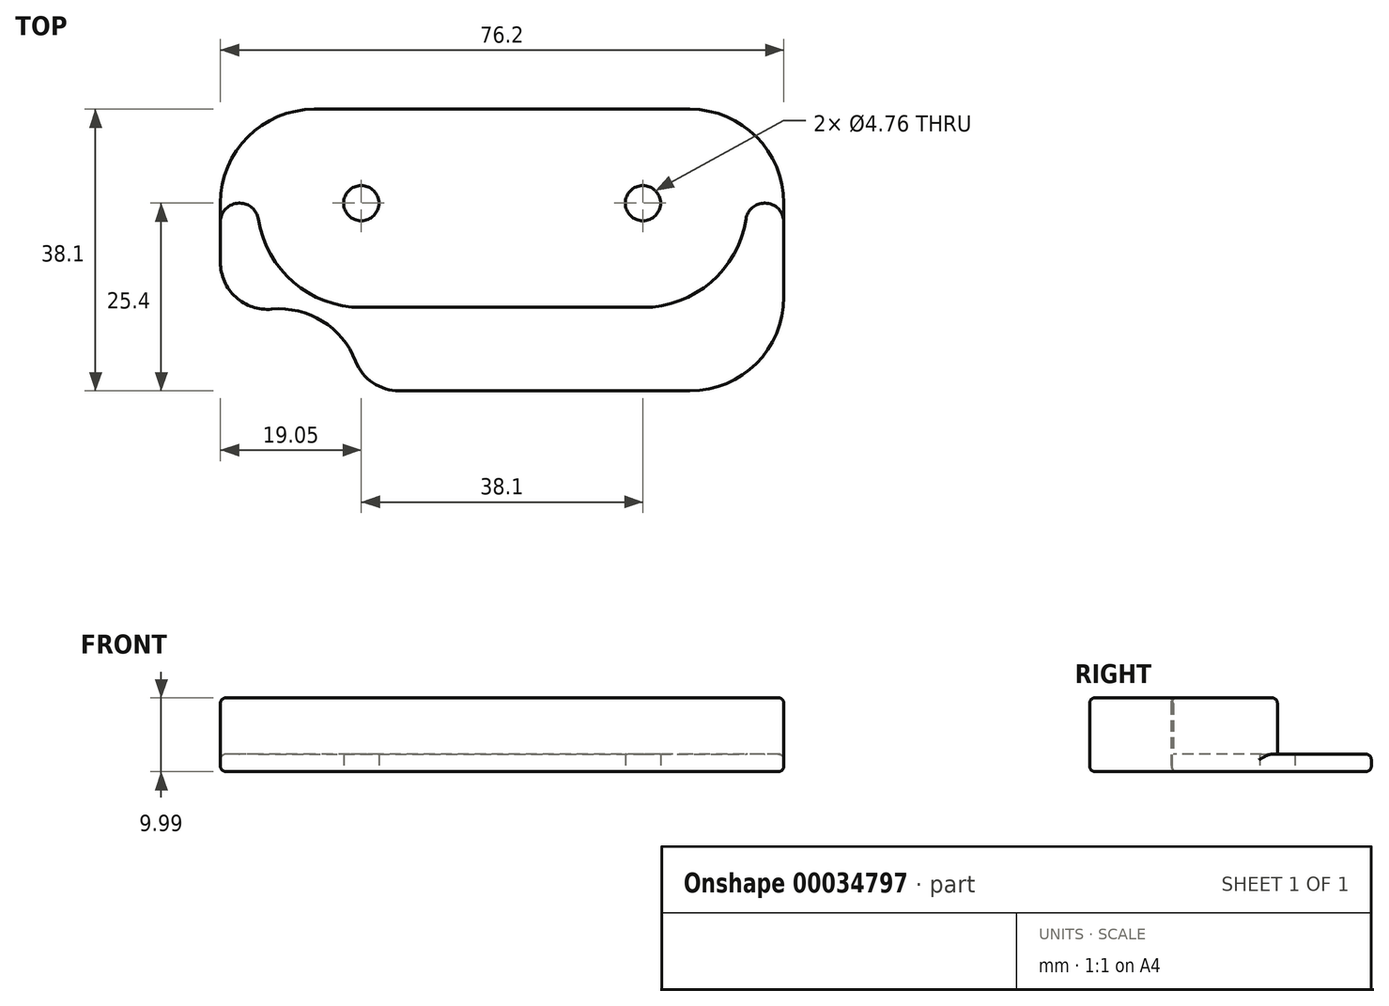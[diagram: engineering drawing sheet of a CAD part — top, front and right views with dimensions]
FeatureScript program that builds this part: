
annotation { "Feature Type Name" : "Feature", "Feature Type Description" : "" }
export const myFeature = defineFeature(function(context is Context, id is Id, definition is map)
    precondition{}
    {
        {
            var Q0;
            Q0=qCreatedBy(makeId("Top.planeOp"),FACE);
            var sketch = newSketch(context, id + "F0", { "sketchPlane" : qUnion([Q0])});
            skLineSegment(sketch, "E0.rect.bottom", {"start": v(25.4, 19.05) * mm, "end": v(-25.4, 19.05) * mm});
            skLineSegment(sketch, "E0.rect.top", {"start": v(25.4, -19.05) * mm, "end": v(-25.4, -19.05) * mm});
            skLineSegment(sketch, "E0.rect.left", {"start": v(38.1, 6.35) * mm, "end": v(38.1, -6.35) * mm});
            skLineSegment(sketch, "E0.rect.right", {"start": v(-38.1, 6.35) * mm, "end": v(-38.1, -6.35) * mm});
            skPoint(sketch, "E0.rect.middle", {"position": v(0, 0) * mm});
            skCircle(sketch, "E1", {"center": v(-19.05, 6.35) * mm, "radius": 13.84 * mm, "construction": true});
            skCircle(sketch, "E2", {"center": v(19.05, 6.35) * mm, "radius": 13.84 * mm, "construction": true});
            skLineSegment(sketch, "E3", {"start": v(-19.05, 6.35) * mm, "end": v(19.05, 6.35) * mm, "construction": true});
            skLineSegment(sketch, "E4", {"start": v(0, 6.35) * mm, "end": v(0, 0) * mm, "construction": true});
            skPoint(sketch, "E5.visualSharp", {"position": v(-38.1, 19.05) * mm});
            skArc(sketch, "E5.filletArc", {"start": v(-25.4, 19.05) * mm, "mid": v(-34.38, 15.33) * mm, "end": v(-38.1, 6.35) * mm});
            skPoint(sketch, "E6.visualSharp", {"position": v(-38.1, -19.05) * mm});
            skArc(sketch, "E6.filletArc", {"start": v(-38.1, -6.35) * mm, "mid": v(-34.38, -15.33) * mm, "end": v(-25.4, -19.05) * mm});
            skPoint(sketch, "E7.visualSharp", {"position": v(38.1, -19.05) * mm});
            skArc(sketch, "E7.filletArc", {"start": v(25.4, -19.05) * mm, "mid": v(34.38, -15.33) * mm, "end": v(38.1, -6.35) * mm});
            skPoint(sketch, "E8.visualSharp", {"position": v(38.1, 19.05) * mm});
            skArc(sketch, "E8.filletArc", {"start": v(38.1, 6.35) * mm, "mid": v(34.38, 15.33) * mm, "end": v(25.4, 19.05) * mm});
            skCircle(sketch, "E9", {"center": v(-19.05, 6.35) * mm, "radius": 2.38 * mm});
            skCircle(sketch, "E10", {"center": v(19.05, 6.35) * mm, "radius": 2.38 * mm});
            skSolve(sketch);
        }
        {
            var Q0;
            Q0=makeQuery(id+"F0.imprint","IMPRINT",FACE,{"disambiguationData":[TD([[makeQuery(id+"F0.imprint","IMPRINT",EDGE,{"derivedFrom":sQuery(id+"F0.wireOp",EDGE,"E0.rect.bottom")}),1.0]])]});
            extrude(context, id + "F1", {"entities" : qUnion([Q0]), "depth" : 2.37 * mm});
        }
        {
            var Q0;
            Q0=makeQuery(id+"F1.opExtrude","CAP_FACE",FACE,{"disambiguationData":[OSD([sQuery(id+"F0.wireOp",EDGE,"E0.rect.bottom"),sQuery(id+"F0.wireOp",EDGE,"E0.rect.top"),sQuery(id+"F0.wireOp",EDGE,"E0.rect.left"),sQuery(id+"F0.wireOp",EDGE,"E0.rect.right"),sQuery(id+"F0.wireOp",EDGE,"E5.filletArc"),sQuery(id+"F0.wireOp",EDGE,"E6.filletArc"),sQuery(id+"F0.wireOp",EDGE,"E7.filletArc"),sQuery(id+"F0.wireOp",EDGE,"E8.filletArc")])],"isStart":false});
            var sketch = newSketch(context, id + "F2", { "sketchPlane" : qUnion([Q0])});
            skArc(sketch, "E11", {"start": v(-32.98, 4.2) * mm, "mid": v(-28.23, -4.35) * mm, "end": v(-19.05, -7.75) * mm});
            skArc(sketch, "E12", {"start": v(19.05, -7.75) * mm, "mid": v(28.23, -4.35) * mm, "end": v(32.98, 4.2) * mm});
            skLineSegment(sketch, "E13", {"start": v(-19.05, -7.75) * mm, "end": v(19.05, -7.75) * mm});
            skLineSegment(sketch, "E14", {"start": v(-35.56, 6.35) * mm, "end": v(-35.5, 6.35) * mm});
            skLineSegment(sketch, "E15.trimOffspring", {"start": v(35.5, 6.35) * mm, "end": v(35.56, 6.35) * mm});
            skLineSegment(sketch, "E16.0", {"start": v(38.1, 3.81) * mm, "end": v(38.1, -6.35) * mm});
            skArc(sketch, "E16.1", {"start": v(25.4, -19.05) * mm, "mid": v(34.38, -15.33) * mm, "end": v(38.1, -6.35) * mm});
            skLineSegment(sketch, "E16.2", {"start": v(25.4, -19.05) * mm, "end": v(-25.4, -19.05) * mm});
            skArc(sketch, "E16.3", {"start": v(-38.1, -6.35) * mm, "mid": v(-34.38, -15.33) * mm, "end": v(-25.4, -19.05) * mm});
            skLineSegment(sketch, "E16.4", {"start": v(-38.1, 3.8) * mm, "end": v(-38.1, -6.35) * mm});
            skLineSegment(sketch, "E17", {"start": v(-62.67, 14.6) * mm, "end": v(-70.33, 1.23) * mm});
            skLineSegment(sketch, "E18", {"start": v(-61.8, 15.21) * mm, "end": v(-36.93, 19.75) * mm});
            skPoint(sketch, "E19.visualSharp", {"position": v(-62.38, 15.1) * mm});
            skArc(sketch, "E19.filletArc", {"start": v(-61.8, 15.21) * mm, "mid": v(-62.3, 15) * mm, "end": v(-62.67, 14.6) * mm});
            skPoint(sketch, "E20.visualSharp", {"position": v(-38.1, 6.35) * mm});
            skArc(sketch, "E20.filletArc", {"start": v(-35.56, 6.35) * mm, "mid": v(-37.36, 5.6) * mm, "end": v(-38.1, 3.8) * mm});
            skPoint(sketch, "E21.visualSharp", {"position": v(-33.15, 6.35) * mm});
            skArc(sketch, "E21.filletArc", {"start": v(-32.98, 4.2) * mm, "mid": v(-33.84, 5.74) * mm, "end": v(-35.5, 6.35) * mm});
            skPoint(sketch, "E22.visualSharp", {"position": v(33.15, 6.35) * mm});
            skArc(sketch, "E22.filletArc", {"start": v(35.5, 6.35) * mm, "mid": v(33.84, 5.74) * mm, "end": v(32.98, 4.2) * mm});
            skPoint(sketch, "E23.visualSharp", {"position": v(38.1, 6.35) * mm});
            skArc(sketch, "E23.filletArc", {"start": v(38.1, 3.81) * mm, "mid": v(37.36, 5.6) * mm, "end": v(35.56, 6.35) * mm});
            skSolve(sketch);
        }
        {
            var Q0;
            Q0 = qSketchRegion(id + "F2", true);
            extrude(context, id + "F3", {"entities" : qUnion([Q0]), "operationType" : NewBodyOperationType.ADD, "depth" : 7.62 * mm});
        }
        {
            var Q0;
            Q0=qCreatedBy(makeId("Top.planeOp"),FACE);
            var sketch = newSketch(context, id + "F4", { "sketchPlane" : qUnion([Q0])});
            skCircle(sketch, "E24.0", {"center": v(-19.05, 6.35) * mm, "radius": 2.38 * mm, "construction": true});
            skCircle(sketch, "E24.1", {"center": v(19.05, 6.35) * mm, "radius": 2.38 * mm, "construction": true});
            skLineSegment(sketch, "E25", {"start": v(-19.05, 6.35) * mm, "end": v(-19.05, -19.05) * mm, "construction": true});
            skLineSegment(sketch, "E26", {"start": v(-19.05, -19.05) * mm, "end": v(-30.16, -19.05) * mm, "construction": true});
            skCircle(sketch, "E27", {"center": v(-30.16, -19.05) * mm, "radius": 11.11 * mm});
            skLineSegment(sketch, "E28", {"start": v(0, 0) * mm, "end": v(0, -31.17) * mm, "construction": true});
            skLineSegment(sketch, "E29.MirrorCS", {"start": v(19.05, -19.05) * mm, "end": v(30.16, -19.05) * mm, "construction": true});
            skLineSegment(sketch, "E30.MirrorCS", {"start": v(19.05, 6.35) * mm, "end": v(19.05, -19.05) * mm, "construction": true});
            skCircle(sketch, "E31.MirrorC", {"center": v(30.16, -19.05) * mm, "radius": 11.11 * mm});
            skSolve(sketch);
        }
        {
            var Q0;
            Q0=makeQuery(id+"F4.imprint","IMPRINT",FACE,{"disambiguationData":[TD([[makeQuery(id+"F4.imprint","IMPRINT",EDGE,{"derivedFrom":sQuery(id+"F4.wireOp",EDGE,"E27")}),1.0]])]});
            var Q1;
            Q1=makeQuery(id+"F4.imprint","IMPRINT",FACE,{"disambiguationData":[TD([[makeQuery(id+"F4.imprint","IMPRINT",EDGE,{"derivedFrom":sQuery(id+"F4.wireOp",EDGE,"E31.MirrorC")}),-1.0]])]});
            extrude(context, id + "F5", {"entities" : qUnion([Q0, Q1]), "operationType" : NewBodyOperationType.REMOVE, "depth" : 25.4 * mm});
        }
        {
            var Q0;
            Q0=makeQuery(id+"F5.boolean.opBoolean","INTERSECT",EDGE,{"derivedFrom":[makeQuery(id+"F3.boolean.opBoolean","MERGE",FACE,{"derivedFrom":[makeQuery(id+"F1.opExtrude","SWEPT_FACE",FACE,{"disambiguationData":[OSD([sQuery(id+"F0.wireOp",EDGE,"E6.filletArc")])]}),makeQuery(id+"F3.opExtrude","SWEPT_FACE",FACE,{"disambiguationData":[OSD([sQuery(id+"F2.wireOp",EDGE,"E16.3")])]})]}),makeQuery(id+"F5.opExtrude","SWEPT_FACE",FACE,{"disambiguationData":[OSD([sQuery(id+"F4.wireOp",EDGE,"E27")])]})]});
            var Q1;
            Q1=makeQuery(id+"F5.boolean.opBoolean","INTERSECT",EDGE,{"derivedFrom":[makeQuery(id+"F3.boolean.opBoolean","MERGE",FACE,{"derivedFrom":[makeQuery(id+"F1.opExtrude","SWEPT_FACE",FACE,{"disambiguationData":[OSD([sQuery(id+"F0.wireOp",EDGE,"E0.rect.top")])]}),makeQuery(id+"F3.opExtrude","SWEPT_FACE",FACE,{"disambiguationData":[OSD([sQuery(id+"F2.wireOp",EDGE,"E16.2")])]})]}),makeQuery(id+"F5.opExtrude","SWEPT_FACE",FACE,{"disambiguationData":[OSD([sQuery(id+"F4.wireOp",EDGE,"E27")])]})]});
            var Q2;
            Q2=makeQuery(id+"F5.boolean.opBoolean","INTERSECT",EDGE,{"derivedFrom":[makeQuery(id+"F3.boolean.opBoolean","MERGE",FACE,{"derivedFrom":[makeQuery(id+"F1.opExtrude","SWEPT_FACE",FACE,{"disambiguationData":[OSD([sQuery(id+"F0.wireOp",EDGE,"E0.rect.top")])]}),makeQuery(id+"F3.opExtrude","SWEPT_FACE",FACE,{"disambiguationData":[OSD([sQuery(id+"F2.wireOp",EDGE,"E16.2")])]})]}),makeQuery(id+"F5.opExtrude","SWEPT_FACE",FACE,{"disambiguationData":[OSD([sQuery(id+"F4.wireOp",EDGE,"E31.MirrorC")])]})]});
            var Q3;
            Q3=makeQuery(id+"F5.boolean.opBoolean","INTERSECT",EDGE,{"derivedFrom":[makeQuery(id+"F3.boolean.opBoolean","MERGE",FACE,{"derivedFrom":[makeQuery(id+"F1.opExtrude","SWEPT_FACE",FACE,{"disambiguationData":[OSD([sQuery(id+"F0.wireOp",EDGE,"E7.filletArc")])]}),makeQuery(id+"F3.opExtrude","SWEPT_FACE",FACE,{"disambiguationData":[OSD([sQuery(id+"F2.wireOp",EDGE,"E16.1")])]})]}),makeQuery(id+"F5.opExtrude","SWEPT_FACE",FACE,{"disambiguationData":[OSD([sQuery(id+"F4.wireOp",EDGE,"E31.MirrorC")])]})]});
            fillet(context, id + "F6", {"entities" : qUnion([Q0, Q1, Q2, Q3]), "radius" : 6.35 * mm, "tangentPropagation" : true, "allowEdgeOverflow" : false});
        }
        {
            var Q0;
            Q0=makeQuery(id+"F3.opExtrude","CAP_FACE",FACE,{"disambiguationData":[OSD([sQuery(id+"F2.wireOp",EDGE,"E11"),sQuery(id+"F2.wireOp",EDGE,"E12"),sQuery(id+"F2.wireOp",EDGE,"E13"),sQuery(id+"F2.wireOp",EDGE,"E14"),sQuery(id+"F2.wireOp",EDGE,"E15.trimOffspring"),sQuery(id+"F2.wireOp",EDGE,"E16.0"),sQuery(id+"F2.wireOp",EDGE,"E16.1"),sQuery(id+"F2.wireOp",EDGE,"E16.2"),sQuery(id+"F2.wireOp",EDGE,"E16.3"),sQuery(id+"F2.wireOp",EDGE,"E16.4"),sQuery(id+"F2.wireOp",EDGE,"E20.filletArc"),sQuery(id+"F2.wireOp",EDGE,"E21.filletArc"),sQuery(id+"F2.wireOp",EDGE,"E22.filletArc"),sQuery(id+"F2.wireOp",EDGE,"E23.filletArc")])],"isStart":false});
            var Q1;
            Q1=makeQuery(id+"F1.opExtrude","CAP_EDGE",EDGE,{"disambiguationData":[OSD([sQuery(id+"F0.wireOp",EDGE,"E0.rect.bottom")])],"isStart":false});
            var Q2;
            Q2=makeQuery(id+"F1.opExtrude","CAP_EDGE",EDGE,{"disambiguationData":[OSD([sQuery(id+"F0.wireOp",EDGE,"E5.filletArc")])],"isStart":false});
            var Q3;
            Q3=makeQuery(id+"F1.opExtrude","CAP_EDGE",EDGE,{"disambiguationData":[OSD([sQuery(id+"F0.wireOp",EDGE,"E0.rect.right")])],"isStart":true});
            fillet(context, id + "F7", {"entities" : qUnion([Q0, Q1, Q2, Q3]), "radius" : 0.76 * mm, "tangentPropagation" : true, "allowEdgeOverflow" : false});
        }
    });
